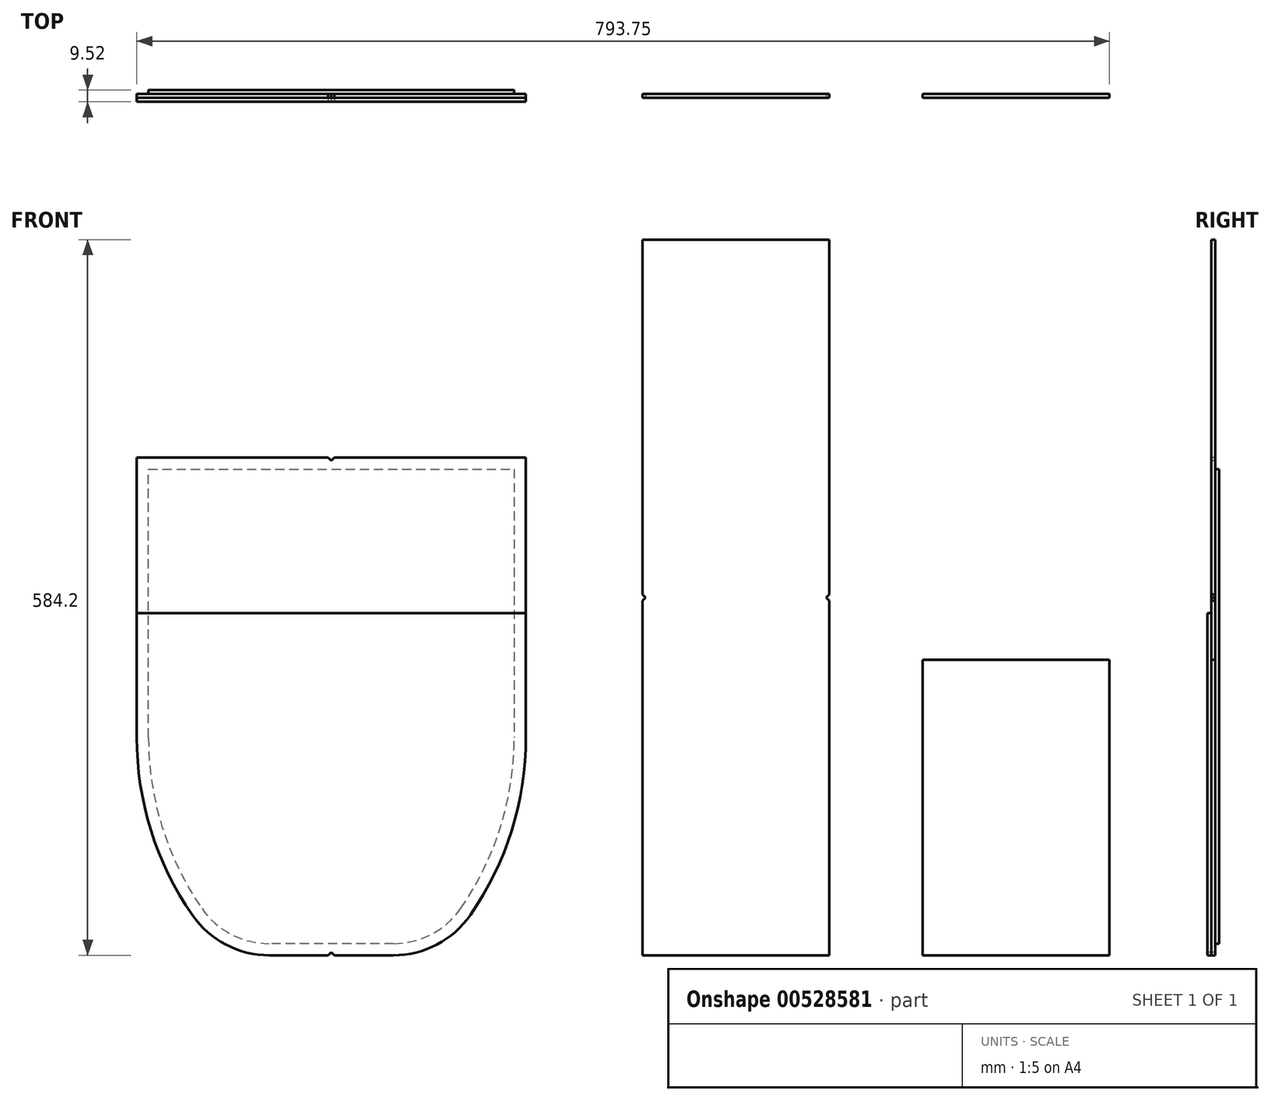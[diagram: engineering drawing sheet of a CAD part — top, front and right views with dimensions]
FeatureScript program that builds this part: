
annotation { "Feature Type Name" : "Feature", "Feature Type Description" : "" }
export const myFeature = defineFeature(function(context is Context, id is Id, definition is map)
    precondition{}
    {
        {
            var Q0;
            Q0=qCreatedBy(makeId("Front.planeOp"),FACE);
            var sketch = newSketch(context, id + "F0", { "sketchPlane" : qUnion([Q0])});
            skLineSegment(sketch, "E0.bottom", {"start": v(158.75, 0) * mm, "end": v(-158.75, 0) * mm, "construction": true});
            skLineSegment(sketch, "E0.top", {"start": v(158.75, 406.4) * mm, "end": v(-158.75, 406.4) * mm});
            skLineSegment(sketch, "E0.left", {"start": v(158.75, 0) * mm, "end": v(158.75, 406.4) * mm, "construction": true});
            skLineSegment(sketch, "E0.right", {"start": v(-158.75, 0) * mm, "end": v(-158.75, 406.4) * mm, "construction": true});
            skPoint(sketch, "E0.middle", {"position": v(0, 203.2) * mm});
            skLineSegment(sketch, "E1", {"start": v(-158.75, 406.4) * mm, "end": v(-158.75, 177.8) * mm});
            skLineSegment(sketch, "E2", {"start": v(0, 0) * mm, "end": v(-50.8, 0) * mm});
            skArc(sketch, "E3", {"start": v(-113.44, 32.81) * mm, "mid": v(-86.16, 8.7) * mm, "end": v(-50.8, 0) * mm});
            skArc(sketch, "E4", {"start": v(-158.75, 177.8) * mm, "mid": v(-147.16, 101.85) * mm, "end": v(-113.44, 32.81) * mm});
            skLineSegment(sketch, "E5", {"start": v(0, 203.2) * mm, "end": v(0, 406.4) * mm, "construction": true});
            skLineSegment(sketch, "E6.MirrorCS", {"start": v(158.75, 406.4) * mm, "end": v(158.75, 177.8) * mm});
            skArc(sketch, "E7.MirrorCS", {"start": v(158.75, 177.8) * mm, "mid": v(147.16, 101.85) * mm, "end": v(113.44, 32.81) * mm});
            skArc(sketch, "E8.MirrorCS", {"start": v(113.44, 32.81) * mm, "mid": v(86.16, 8.7) * mm, "end": v(50.8, 0) * mm});
            skLineSegment(sketch, "E9.MirrorCS", {"start": v(0, 0) * mm, "end": v(50.8, 0) * mm});
            skSolve(sketch);
        }
        {
            var Q0;
            Q0 = qSketchRegion(id + "F0", true);
            extrude(context, id + "F1", {"entities" : qUnion([Q0]), "depth" : 3.17 * mm, "offsetDistance" : 25.4 * mm});
        }
        {
            var Q0;
            Q0=makeQuery(id+"F1.opExtrude","CAP_FACE",FACE,{"disambiguationData":[OSD([sQuery(id+"F0.wireOp",EDGE,"E0.top"),sQuery(id+"F0.wireOp",EDGE,"E1"),sQuery(id+"F0.wireOp",EDGE,"E2"),sQuery(id+"F0.wireOp",EDGE,"E3"),sQuery(id+"F0.wireOp",EDGE,"E4"),sQuery(id+"F0.wireOp",EDGE,"E6.MirrorCS"),sQuery(id+"F0.wireOp",EDGE,"E7.MirrorCS"),sQuery(id+"F0.wireOp",EDGE,"E8.MirrorCS"),sQuery(id+"F0.wireOp",EDGE,"E9.MirrorCS")])],"isStart":false});
            var sketch = newSketch(context, id + "F2", { "sketchPlane" : qUnion([Q0])});
            skArc(sketch, "E10.0.0", {"start": v(-158.75, 177.8) * mm, "mid": v(-147.16, 101.85) * mm, "end": v(-113.44, 32.81) * mm});
            skArc(sketch, "E10.0.1", {"start": v(-113.44, 32.81) * mm, "mid": v(-86.16, 8.7) * mm, "end": v(-50.8, 0) * mm});
            skLineSegment(sketch, "E10.0.2", {"start": v(-50.8, 0) * mm, "end": v(50.8, 0) * mm});
            skArc(sketch, "E10.0.3", {"start": v(50.8, 0) * mm, "mid": v(86.16, 8.7) * mm, "end": v(113.44, 32.81) * mm});
            skArc(sketch, "E10.0.4", {"start": v(113.44, 32.81) * mm, "mid": v(147.16, 101.85) * mm, "end": v(158.75, 177.8) * mm});
            skLineSegment(sketch, "E10.0.5", {"start": v(158.75, 177.8) * mm, "end": v(158.75, 279.4) * mm});
            skLineSegment(sketch, "E10.0.7", {"start": v(-158.75, 279.4) * mm, "end": v(-158.75, 177.8) * mm});
            skLineSegment(sketch, "E11", {"start": v(-158.75, 279.4) * mm, "end": v(158.75, 279.4) * mm});
            skPoint(sketch, "E10.0.6.start.orphan", {"position": v(158.75, 406.4) * mm});
            skPoint(sketch, "E12.orphan", {"position": v(-158.75, 406.4) * mm});
            skSolve(sketch);
        }
        {
            var Q0;
            Q0 = qSketchRegion(id + "F2", true);
            extrude(context, id + "F3", {"entities" : qUnion([Q0]), "depth" : 3.17 * mm, "offsetDistance" : 25.4 * mm});
        }
        {
            var Q0;
            Q0=makeQuery(id+"F1.opExtrude","CAP_FACE",FACE,{"disambiguationData":[OSD([sQuery(id+"F0.wireOp",EDGE,"E0.top"),sQuery(id+"F0.wireOp",EDGE,"E1"),sQuery(id+"F0.wireOp",EDGE,"E2"),sQuery(id+"F0.wireOp",EDGE,"E3"),sQuery(id+"F0.wireOp",EDGE,"E4"),sQuery(id+"F0.wireOp",EDGE,"E6.MirrorCS"),sQuery(id+"F0.wireOp",EDGE,"E7.MirrorCS"),sQuery(id+"F0.wireOp",EDGE,"E8.MirrorCS"),sQuery(id+"F0.wireOp",EDGE,"E9.MirrorCS")])],"isStart":true});
            var sketch = newSketch(context, id + "F4", { "sketchPlane" : qUnion([Q0])});
            skArc(sketch, "E13.0", {"start": v(50.8, 9.53) * mm, "mid": v(81.74, 17.14) * mm, "end": v(105.61, 38.24) * mm});
            skLineSegment(sketch, "E13.1", {"start": v(-50.8, 9.53) * mm, "end": v(50.8, 9.53) * mm});
            skArc(sketch, "E13.2", {"start": v(105.61, 38.24) * mm, "mid": v(138.07, 104.69) * mm, "end": v(149.22, 177.8) * mm});
            skArc(sketch, "E13.3", {"start": v(-105.61, 38.24) * mm, "mid": v(-81.74, 17.14) * mm, "end": v(-50.8, 9.52) * mm});
            skLineSegment(sketch, "E13.4", {"start": v(149.22, 177.8) * mm, "end": v(149.22, 396.88) * mm});
            skLineSegment(sketch, "E13.5", {"start": v(149.22, 396.88) * mm, "end": v(-149.22, 396.88) * mm});
            skLineSegment(sketch, "E13.6", {"start": v(-149.22, 396.88) * mm, "end": v(-149.22, 177.8) * mm});
            skArc(sketch, "E13.7", {"start": v(-149.22, 177.8) * mm, "mid": v(-138.07, 104.69) * mm, "end": v(-105.61, 38.24) * mm});
            skSolve(sketch);
        }
        {
            var Q0;
            Q0 = qSketchRegion(id + "F4", true);
            extrude(context, id + "F5", {"entities" : qUnion([Q0]), "depth" : 3.17 * mm, "offsetDistance" : 25.4 * mm});
        }
        {
            var Q0;
            Q0=qCreatedBy(makeId("Front.planeOp"),FACE);
            var sketch = newSketch(context, id + "F6", { "sketchPlane" : qUnion([Q0])});
            skLineSegment(sketch, "E14.bottom", {"start": v(254, 0) * mm, "end": v(406.4, 0) * mm});
            skLineSegment(sketch, "E14.top", {"start": v(254, 584.2) * mm, "end": v(406.4, 584.2) * mm});
            skLineSegment(sketch, "E14.left", {"start": v(254, 0) * mm, "end": v(254, 584.2) * mm});
            skLineSegment(sketch, "E14.right", {"start": v(406.4, 0) * mm, "end": v(406.4, 584.2) * mm});
            skLineSegment(sketch, "E15.bottom", {"start": v(482.6, 0) * mm, "end": v(635, 0) * mm});
            skLineSegment(sketch, "E15.top", {"start": v(482.6, 241.3) * mm, "end": v(635, 241.3) * mm});
            skLineSegment(sketch, "E15.left", {"start": v(482.6, 0) * mm, "end": v(482.6, 241.3) * mm});
            skLineSegment(sketch, "E15.right", {"start": v(635, 0) * mm, "end": v(635, 241.3) * mm});
            skSolve(sketch);
        }
        {
            var Q0;
            Q0 = qSketchRegion(id + "F6", true);
            extrude(context, id + "F7", {"entities" : qUnion([Q0]), "depth" : 3.17 * mm, "offsetDistance" : 25.4 * mm});
        }
        {
            var Q0;
            Q0=makeQuery(id+"F3.opExtrude","CAP_FACE",FACE,{"disambiguationData":[OSD([sQuery(id+"F2.wireOp",EDGE,"E10.0.0"),sQuery(id+"F2.wireOp",EDGE,"E10.0.1"),sQuery(id+"F2.wireOp",EDGE,"E10.0.2"),sQuery(id+"F2.wireOp",EDGE,"E10.0.3"),sQuery(id+"F2.wireOp",EDGE,"E10.0.4"),sQuery(id+"F2.wireOp",EDGE,"E10.0.5"),sQuery(id+"F2.wireOp",EDGE,"E10.0.7"),sQuery(id+"F2.wireOp",EDGE,"E11")])],"isStart":false});
            var sketch = newSketch(context, id + "F8", { "sketchPlane" : qUnion([Q0])});
            skLineSegment(sketch, "E16", {"start": v(-2.54, 0) * mm, "end": v(0, 2.54) * mm});
            skLineSegment(sketch, "E17", {"start": v(0, 2.54) * mm, "end": v(2.54, 0) * mm});
            skLineSegment(sketch, "E18", {"start": v(2.54, 0) * mm, "end": v(-2.54, 0) * mm});
            skLineSegment(sketch, "E19", {"start": v(0, 0) * mm, "end": v(0, 19.86) * mm, "construction": true});
            skLineSegment(sketch, "E20", {"start": v(386.73, 292.1) * mm, "end": v(406.4, 292.1) * mm, "construction": true});
            skLineSegment(sketch, "E21", {"start": v(406.4, 294.64) * mm, "end": v(403.86, 292.1) * mm});
            skLineSegment(sketch, "E22", {"start": v(403.86, 292.1) * mm, "end": v(406.4, 289.56) * mm});
            skLineSegment(sketch, "E23", {"start": v(406.4, 289.56) * mm, "end": v(406.4, 294.64) * mm});
            skLineSegment(sketch, "E24", {"start": v(330.2, 584.2) * mm, "end": v(330.2, 504.91) * mm, "construction": true});
            skLineSegment(sketch, "E25.MirrorCS", {"start": v(254, 294.64) * mm, "end": v(256.54, 292.1) * mm});
            skLineSegment(sketch, "E26.MirrorCS", {"start": v(256.54, 292.1) * mm, "end": v(254, 289.56) * mm});
            skLineSegment(sketch, "E27.MirrorCS", {"start": v(254, 289.56) * mm, "end": v(254, 294.64) * mm});
            skLineSegment(sketch, "E28", {"start": v(0, 406.4) * mm, "end": v(0, 372.55) * mm, "construction": true});
            skLineSegment(sketch, "E29", {"start": v(-2.54, 406.4) * mm, "end": v(0, 403.86) * mm});
            skLineSegment(sketch, "E30", {"start": v(0, 403.86) * mm, "end": v(2.54, 406.4) * mm});
            skLineSegment(sketch, "E31", {"start": v(2.54, 406.4) * mm, "end": v(-2.54, 406.4) * mm});
            skSolve(sketch);
        }
        {
            var Q0;
            Q0 = qSketchRegion(id + "F8", true);
            extrude(context, id + "F9", {"entities" : qUnion([Q0]), "operationType" : NewBodyOperationType.REMOVE, "oppositeDirection" : true, "depth" : 25.4 * mm, "offsetDistance" : 25.4 * mm});
        }
    });
